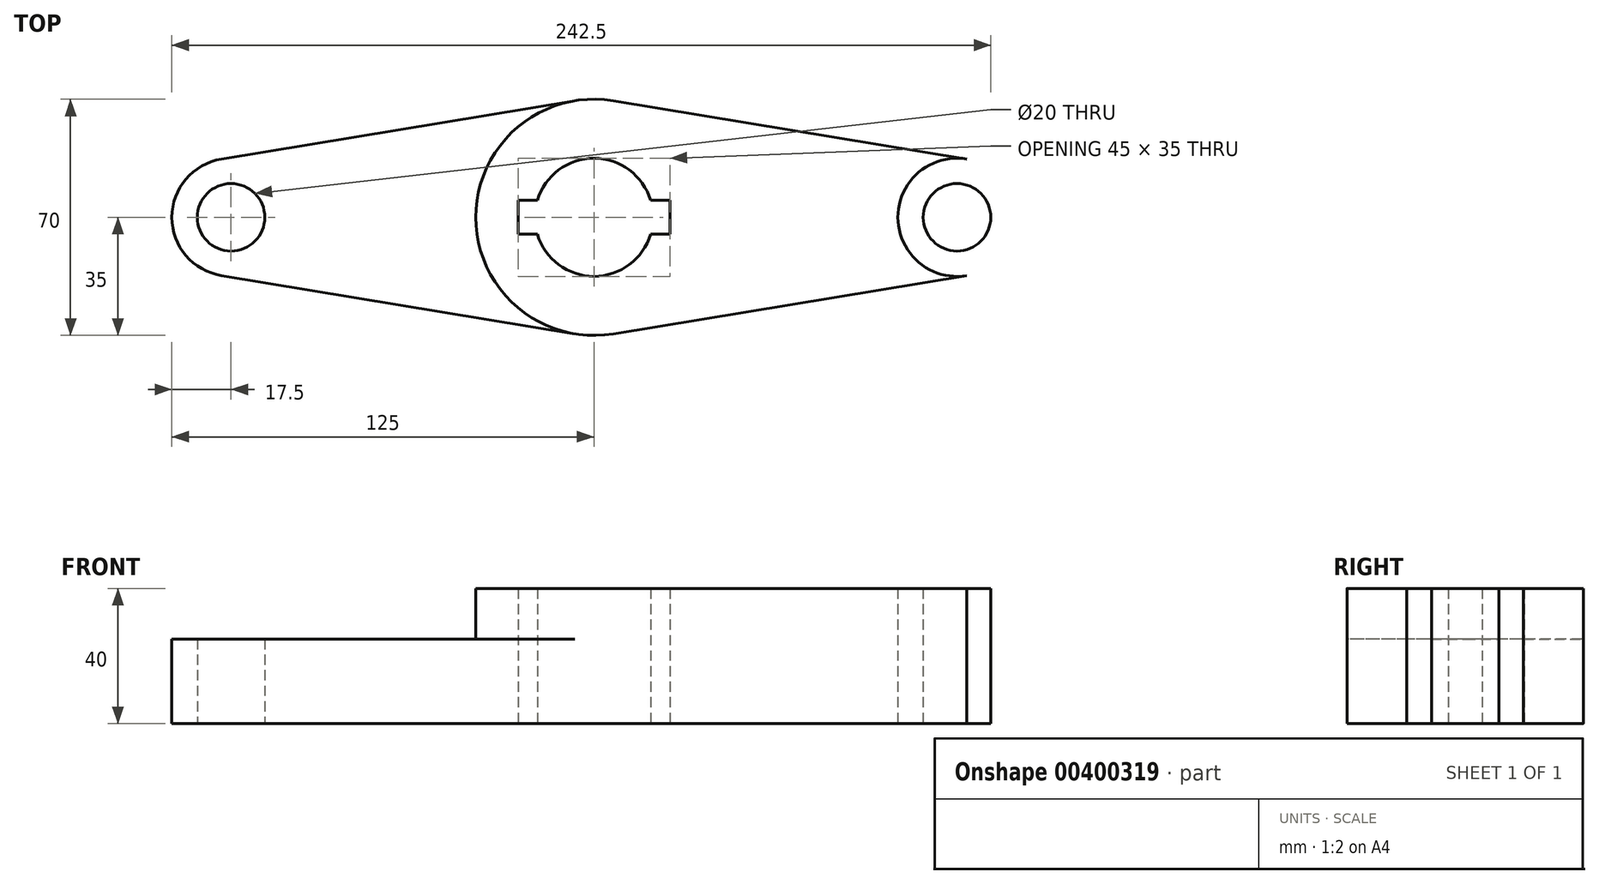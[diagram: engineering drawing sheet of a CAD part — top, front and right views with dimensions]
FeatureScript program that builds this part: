
annotation { "Feature Type Name" : "Feature", "Feature Type Description" : "" }
export const myFeature = defineFeature(function(context is Context, id is Id, definition is map)
    precondition{}
    {
        {
            var Q0;
            Q0=qCreatedBy(makeId("Top.planeOp"),FACE);
            var sketch = newSketch(context, id + "F0", { "sketchPlane" : qUnion([Q0])});
            skCircle(sketch, "E0", {"center": v(0, 0) * mm, "radius": 35 * mm});
            skCircle(sketch, "E1", {"center": v(0, 0) * mm, "radius": 17.5 * mm});
            skCircle(sketch, "E2", {"center": v(-107.5, 0) * mm, "radius": 17.5 * mm});
            skCircle(sketch, "E3", {"center": v(-107.5, 0) * mm, "radius": 10 * mm});
            skLineSegment(sketch, "E4", {"start": v(-110.35, 17.27) * mm, "end": v(-5.7, 34.53) * mm});
            skLineSegment(sketch, "E5", {"start": v(0, 0) * mm, "end": v(0, 55.66) * mm, "construction": true});
            skLineSegment(sketch, "E6", {"start": v(0, 0) * mm, "end": v(-146.4, 0) * mm, "construction": true});
            skLineSegment(sketch, "E7.MirrorCS", {"start": v(-110.35, -17.27) * mm, "end": v(-5.7, -34.53) * mm});
            skLineSegment(sketch, "E8.MirrorCS", {"start": v(110.35, 17.27) * mm, "end": v(5.7, 34.53) * mm});
            skCircle(sketch, "E9.MirrorC", {"center": v(107.5, 0) * mm, "radius": 17.5 * mm});
            skCircle(sketch, "E10.MirrorC", {"center": v(107.5, 0) * mm, "radius": 10 * mm});
            skLineSegment(sketch, "E11.MirrorCS", {"start": v(110.35, -17.27) * mm, "end": v(5.7, -34.53) * mm});
            skLineSegment(sketch, "E12.bottom", {"start": v(22.5, 5) * mm, "end": v(-22.5, 5) * mm});
            skLineSegment(sketch, "E12.top", {"start": v(22.5, -5) * mm, "end": v(-22.5, -5) * mm});
            skLineSegment(sketch, "E12.left", {"start": v(22.5, 5) * mm, "end": v(22.5, -5) * mm});
            skLineSegment(sketch, "E12.right", {"start": v(-22.5, 5) * mm, "end": v(-22.5, -5) * mm});
            skSolve(sketch);
        }
        {
            var Q0;
            {var subQ3=sQuery(id+"F0.wireOp",EDGE,"E8.MirrorCS");Q0=makeQuery(id+"F0.imprint","IMPRINT",FACE,{"disambiguationData":[TD([[makeQuery(id+"F0.imprint","IMPRINT",EDGE,{"derivedFrom":subQ3}),1.0]])]});}
            var Q1;
            Q1=makeQuery(id+"F0.imprint","IMPRINT",FACE,{"disambiguationData":[TD([[makeQuery(id+"F0.imprint","IMPRINT",EDGE,{"derivedFrom":sQuery(id+"F0.wireOp",EDGE,"E10.MirrorC")}),1.0]])]});
            var Q2;
            {var subQ12=sQuery(id+"F0.wireOp",EDGE,"E12.left");Q2=makeQuery(id+"F0.imprint","IMPRINT",FACE,{"disambiguationData":[TD([[makeQuery(id+"F0.imprint","IMPRINT",EDGE,{"derivedFrom":subQ12}),1.0]])]});}
            extrude(context, id + "F1", {"entities" : qUnion([Q0, Q1, Q2]), "depth" : 40 * mm, "offsetDistance" : 25 * mm});
        }
        {
            var Q0;
            {var subQ0=sQuery(id+"F0.wireOp",EDGE,"E4");Q0=makeQuery(id+"F0.imprint","IMPRINT",FACE,{"disambiguationData":[TD([[makeQuery(id+"F0.imprint","IMPRINT",EDGE,{"derivedFrom":subQ0}),-1.0]])]});}
            var Q1;
            Q1=makeQuery(id+"F0.imprint","IMPRINT",FACE,{"disambiguationData":[TD([[makeQuery(id+"F0.imprint","IMPRINT",EDGE,{"derivedFrom":sQuery(id+"F0.wireOp",EDGE,"E3")}),-1.0]])]});
            extrude(context, id + "F2", {"entities" : qUnion([Q0, Q1]), "operationType" : NewBodyOperationType.ADD, "depth" : 25 * mm, "offsetDistance" : 25 * mm});
        }
    });
